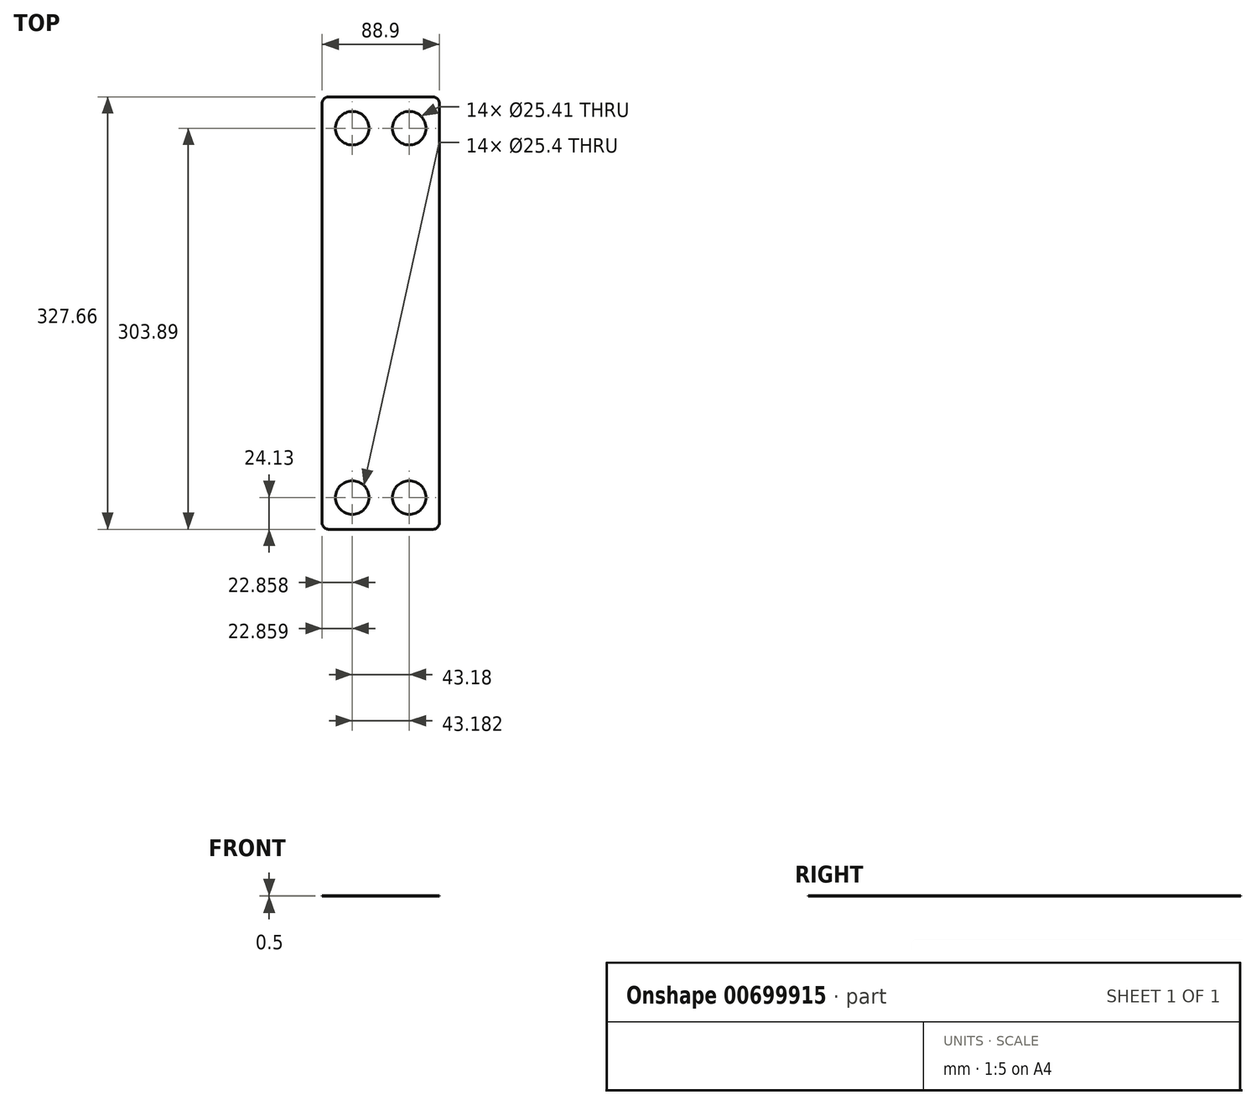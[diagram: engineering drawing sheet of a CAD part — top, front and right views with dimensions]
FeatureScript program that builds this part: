
annotation { "Feature Type Name" : "Feature", "Feature Type Description" : "" }
export const myFeature = defineFeature(function(context is Context, id is Id, definition is map)
    precondition{}
    {
        {
            var Q0;
            Q0=qCreatedBy(makeId("Top.planeOp"),FACE);
            var sketch = newSketch(context, id + "F0", { "sketchPlane" : qUnion([Q0])});
            skLineSegment(sketch, "E0.bottom", {"start": v(43.82, 174) * mm, "end": v(-45.08, 174) * mm});
            skLineSegment(sketch, "E0.top", {"start": v(43.82, -153.66) * mm, "end": v(-45.08, -153.66) * mm});
            skLineSegment(sketch, "E0.left", {"start": v(43.82, 174) * mm, "end": v(43.82, -153.66) * mm});
            skLineSegment(sketch, "E0.right", {"start": v(-45.08, 174) * mm, "end": v(-45.08, -153.66) * mm});
            skPoint(sketch, "E1", {"position": v(-22.22, 149.87) * mm});
            skPoint(sketch, "E2", {"position": v(20.96, 149.87) * mm});
            skPoint(sketch, "E3", {"position": v(-19.26, -129.53) * mm});
            skCircle(sketch, "E4.MirrorC", {"center": v(20.96, 150.23) * mm, "radius": 12.7 * mm});
            skCircle(sketch, "E5.MirrorC", {"center": v(-22.22, -129.53) * mm, "radius": 12.7 * mm});
            skCircle(sketch, "E6.MirrorC", {"center": v(-22.22, 150.23) * mm, "radius": 12.7 * mm});
            skCircle(sketch, "E7.MirrorC", {"center": v(20.96, -129.53) * mm, "radius": 12.7 * mm});
            skSolve(sketch);
        }
        {
            var Q0;
            Q0=makeQuery(id+"F0.imprint","IMPRINT",FACE,{"disambiguationData":[TD([[makeQuery(id+"F0.imprint","IMPRINT",EDGE,{"derivedFrom":sQuery(id+"F0.wireOp",EDGE,"E0.bottom")}),1.0]])]});
            extrude(context, id + "F1", {"entities" : qUnion([Q0]), "depth" : 0.5 * mm, "offsetDistance" : 25.4 * mm});
        }
        {
            var Q0;
            Q0=makeQuery(id+"F1.opExtrude","SWEPT_EDGE",EDGE,{"disambiguationData":[OSD([sQuery(id+"F0.wireOp",EDGE,"E0.bottom"),sQuery(id+"F0.wireOp",EDGE,"E0.right")])]});
            var Q1;
            Q1=makeQuery(id+"F1.opExtrude","SWEPT_EDGE",EDGE,{"disambiguationData":[OSD([sQuery(id+"F0.wireOp",EDGE,"E0.bottom"),sQuery(id+"F0.wireOp",EDGE,"E0.left")])]});
            var Q2;
            Q2=makeQuery(id+"F1.opExtrude","SWEPT_EDGE",EDGE,{"disambiguationData":[OSD([sQuery(id+"F0.wireOp",EDGE,"E0.top"),sQuery(id+"F0.wireOp",EDGE,"E0.left")])]});
            var Q3;
            Q3=makeQuery(id+"F1.opExtrude","SWEPT_EDGE",EDGE,{"disambiguationData":[OSD([sQuery(id+"F0.wireOp",EDGE,"E0.top"),sQuery(id+"F0.wireOp",EDGE,"E0.right")])]});
            fillet(context, id + "F2", {"entities" : qUnion([Q0, Q1, Q2, Q3]), "radius" : 5.08 * mm, "tangentPropagation" : true, "allowEdgeOverflow" : false});
        }
    });
